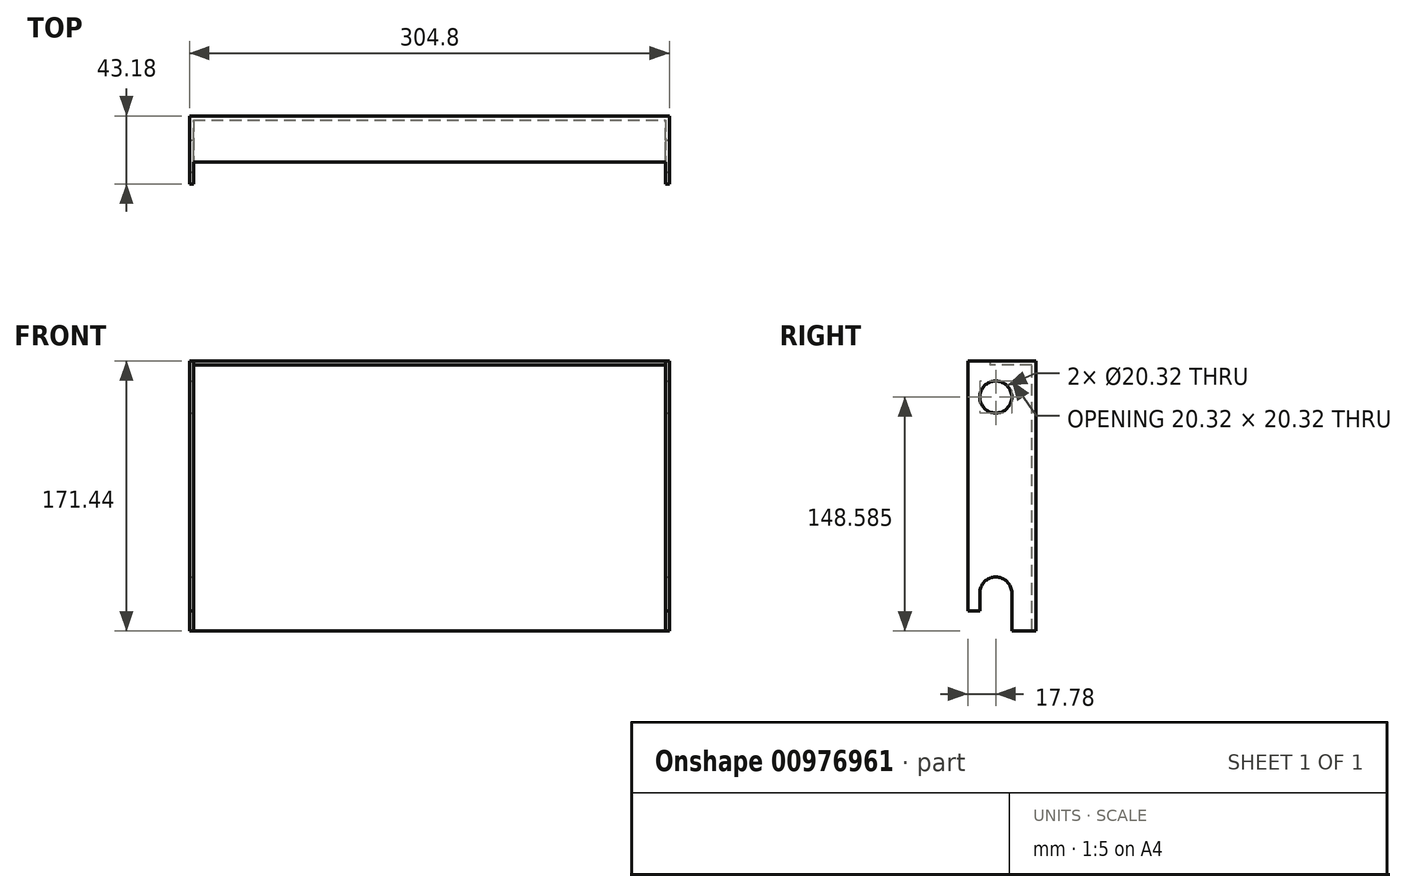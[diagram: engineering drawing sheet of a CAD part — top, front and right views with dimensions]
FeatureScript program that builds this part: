
annotation { "Feature Type Name" : "Feature", "Feature Type Description" : "" }
export const myFeature = defineFeature(function(context is Context, id is Id, definition is map)
    precondition{}
    {
        {
            var Q0;
            Q0=qCreatedBy(makeId("Front.planeOp"),FACE);
            var sketch = newSketch(context, id + "F0", { "sketchPlane" : qUnion([Q0])});
            skLineSegment(sketch, "E0.bottom", {"start": v(-152.4, 85.73) * mm, "end": v(152.4, 85.72) * mm});
            skLineSegment(sketch, "E0.top", {"start": v(-152.4, -85.72) * mm, "end": v(152.4, -85.73) * mm});
            skLineSegment(sketch, "E0.left", {"start": v(-152.4, 85.73) * mm, "end": v(-152.4, -85.73) * mm});
            skLineSegment(sketch, "E0.right", {"start": v(152.4, 85.73) * mm, "end": v(152.4, -85.73) * mm});
            skSolve(sketch);
        }
        {
            var Q0;
            Q0 = qSketchRegion(id + "F0", true);
            extrude(context, id + "F1", {"entities" : qUnion([Q0]), "endBound" : BoundingType.SYMMETRIC, "depth" : 2.54 * mm, "offsetDistance" : 25.4 * mm});
        }
        {
            var Q0;
            Q0=makeQuery(id+"F1.opExtrude","CAP_FACE",FACE,{"disambiguationData":[OSD([sQuery(id+"F0.wireOp",EDGE,"E0.bottom"),sQuery(id+"F0.wireOp",EDGE,"E0.top"),sQuery(id+"F0.wireOp",EDGE,"E0.left"),sQuery(id+"F0.wireOp",EDGE,"E0.right")])],"isStart":false});
            var sketch = newSketch(context, id + "F2", { "sketchPlane" : qUnion([Q0])});
            skLineSegment(sketch, "E1.bottom", {"start": v(-152.4, 85.73) * mm, "end": v(152.4, 85.73) * mm});
            skLineSegment(sketch, "E1.top", {"start": v(-152.4, 83.18) * mm, "end": v(152.4, 83.18) * mm});
            skLineSegment(sketch, "E1.left", {"start": v(-152.4, 85.73) * mm, "end": v(-152.4, 83.18) * mm});
            skLineSegment(sketch, "E1.right", {"start": v(152.4, 85.73) * mm, "end": v(152.4, 83.18) * mm});
            skSolve(sketch);
        }
        {
            var Q0;
            Q0 = qSketchRegion(id + "F2", true);
            extrude(context, id + "F3", {"entities" : qUnion([Q0]), "operationType" : NewBodyOperationType.ADD, "depth" : 26.67 * mm, "offsetDistance" : 25.4 * mm});
        }
        {
            var Q0;
            Q0=makeQuery(id+"F1.opExtrude","CAP_FACE",FACE,{"disambiguationData":[OSD([sQuery(id+"F0.wireOp",EDGE,"E0.bottom"),sQuery(id+"F0.wireOp",EDGE,"E0.top"),sQuery(id+"F0.wireOp",EDGE,"E0.left"),sQuery(id+"F0.wireOp",EDGE,"E0.right")])],"isStart":false});
            var sketch = newSketch(context, id + "F4", { "sketchPlane" : qUnion([Q0])});
            skLineSegment(sketch, "E2.bottom", {"start": v(-152.4, -85.73) * mm, "end": v(-149.86, -85.73) * mm});
            skLineSegment(sketch, "E2.top", {"start": v(-152.4, 85.73) * mm, "end": v(-149.86, 85.73) * mm});
            skLineSegment(sketch, "E2.left", {"start": v(-152.4, -85.73) * mm, "end": v(-152.4, 85.73) * mm});
            skLineSegment(sketch, "E2.right", {"start": v(-149.86, -85.73) * mm, "end": v(-149.86, 85.73) * mm});
            skLineSegment(sketch, "E3.bottom", {"start": v(152.4, -85.73) * mm, "end": v(149.86, -85.73) * mm});
            skLineSegment(sketch, "E3.top", {"start": v(152.4, 85.73) * mm, "end": v(149.86, 85.73) * mm});
            skLineSegment(sketch, "E3.left", {"start": v(152.4, -85.73) * mm, "end": v(152.4, 85.73) * mm});
            skLineSegment(sketch, "E3.right", {"start": v(149.86, -85.73) * mm, "end": v(149.86, 85.72) * mm});
            skSolve(sketch);
        }
        {
            var Q0;
            Q0 = qSketchRegion(id + "F4", true);
            extrude(context, id + "F5", {"entities" : qUnion([Q0]), "operationType" : NewBodyOperationType.ADD, "depth" : 40.64 * mm, "offsetDistance" : 25.4 * mm});
        }
        {
            var Q0;
            Q0=makeQuery(id+"F5.boolean.opBoolean","MERGE",FACE,{"derivedFrom":[makeQuery(id+"F3.boolean.opBoolean","MERGE",FACE,{"derivedFrom":[makeQuery(id+"F1.opExtrude","SWEPT_FACE",FACE,{"disambiguationData":[OSD([sQuery(id+"F0.wireOp",EDGE,"E0.right")])]}),makeQuery(id+"F3.opExtrude","SWEPT_FACE",FACE,{"disambiguationData":[OSD([sQuery(id+"F2.wireOp",EDGE,"E1.right")])]})]}),makeQuery(id+"F5.opExtrude","SWEPT_FACE",FACE,{"disambiguationData":[OSD([sQuery(id+"F4.wireOp",EDGE,"E3.left")])]})]});
            var sketch = newSketch(context, id + "F6", { "sketchPlane" : qUnion([Q0])});
            skCircle(sketch, "E4", {"center": v(-24.13, 62.86) * mm, "radius": 10.16 * mm});
            skLineSegment(sketch, "E5", {"start": v(-41.91, -73.03) * mm, "end": v(-34.3, -73.03) * mm});
            skLineSegment(sketch, "E6", {"start": v(-24.13, 62.86) * mm, "end": v(-24.13, -61.6) * mm, "construction": true});
            skArc(sketch, "E7", {"start": v(-13.97, -61.6) * mm, "mid": v(-24.13, -51.44) * mm, "end": v(-34.3, -61.6) * mm});
            skLineSegment(sketch, "E8", {"start": v(-34.3, -73.03) * mm, "end": v(-34.3, -61.6) * mm});
            skLineSegment(sketch, "E9", {"start": v(-34.3, -61.6) * mm, "end": v(-13.97, -61.6) * mm, "construction": true});
            skLineSegment(sketch, "E10", {"start": v(-13.97, -61.6) * mm, "end": v(-13.97, -85.73) * mm});
            skLineSegment(sketch, "E11", {"start": v(-13.97, -85.73) * mm, "end": v(-41.91, -85.73) * mm});
            skLineSegment(sketch, "E12", {"start": v(-41.91, -85.73) * mm, "end": v(-41.91, -73.03) * mm});
            skSolve(sketch);
        }
        {
            var Q0;
            Q0 = qSketchRegion(id + "F6", true);
            extrude(context, id + "F7", {"entities" : qUnion([Q0]), "operationType" : NewBodyOperationType.REMOVE, "endBound" : BoundingType.THROUGH_ALL, "oppositeDirection" : true, "depth" : 25.4 * mm, "offsetDistance" : 25.4 * mm});
        }
    });
